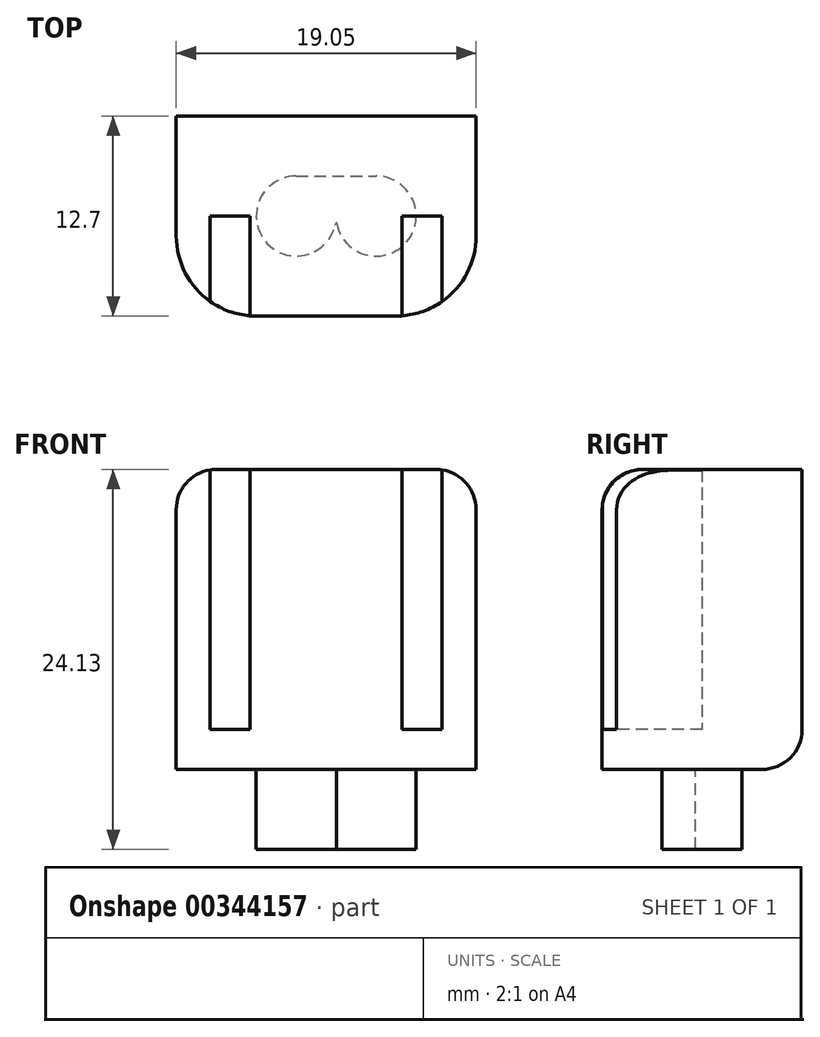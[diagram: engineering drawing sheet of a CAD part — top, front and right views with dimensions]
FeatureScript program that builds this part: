
annotation { "Feature Type Name" : "Feature", "Feature Type Description" : "" }
export const myFeature = defineFeature(function(context is Context, id is Id, definition is map)
    precondition{}
    {
        {
            var Q0;
            Q0=qCreatedBy(makeId("Front.planeOp"),FACE);
            var sketch = newSketch(context, id + "F0", { "sketchPlane" : qUnion([Q0])});
            skLineSegment(sketch, "E0", {"start": v(-9.43, 0) * mm, "end": v(9.62, 0) * mm});
            skLineSegment(sketch, "E1", {"start": v(9.62, 0) * mm, "end": v(9.62, 19.05) * mm});
            skLineSegment(sketch, "E2", {"start": v(9.62, 19.05) * mm, "end": v(-9.43, 19.05) * mm});
            skLineSegment(sketch, "E3", {"start": v(-9.43, 19.05) * mm, "end": v(-9.43, 0) * mm});
            skSolve(sketch);
        }
        {
            var Q0;
            Q0=makeQuery(id+"F0.imprint","IMPRINT",FACE,{"disambiguationData":[TD([[makeQuery(id+"F0.imprint","IMPRINT",EDGE,{"derivedFrom":sQuery(id+"F0.wireOp",EDGE,"E0")}),1.0]])]});
            extrude(context, id + "F1", {"entities" : qUnion([Q0]), "depth" : 12.7 * mm});
        }
        {
            var Q0;
            Q0=makeQuery(id+"F1.opExtrude","SWEPT_EDGE",EDGE,{"disambiguationData":[OSD([sQuery(id+"F0.wireOp",EDGE,"E1"),sQuery(id+"F0.wireOp",EDGE,"E2")])]});
            var Q1;
            Q1=makeQuery(id+"F1.opExtrude","SWEPT_EDGE",EDGE,{"disambiguationData":[OSD([sQuery(id+"F0.wireOp",EDGE,"E2"),sQuery(id+"F0.wireOp",EDGE,"E3")])]});
            var Q2;
            Q2=makeQuery(id+"F1.opExtrude","CAP_EDGE",EDGE,{"disambiguationData":[OSD([sQuery(id+"F0.wireOp",EDGE,"E2")])],"isStart":false});
            fillet(context, id + "F2", {"entities" : qUnion([Q0, Q1, Q2]), "radius" : 2.54 * mm, "tangentPropagation" : true, "allowEdgeOverflow" : false});
        }
        {
            var Q0;
            Q0=makeQuery(id+"F1.opExtrude","CAP_EDGE",EDGE,{"disambiguationData":[OSD([sQuery(id+"F0.wireOp",EDGE,"E1")])],"isStart":false});
            var Q1;
            Q1=makeQuery(id+"F1.opExtrude","CAP_EDGE",EDGE,{"disambiguationData":[OSD([sQuery(id+"F0.wireOp",EDGE,"E3")])],"isStart":false});
            fillet(context, id + "F3", {"entities" : qUnion([Q0, Q1]), "radius" : 5.08 * mm, "tangentPropagation" : true, "allowEdgeOverflow" : false});
        }
        {
            var Q0;
            Q0=makeQuery(id+"F1.opExtrude","CAP_FACE",FACE,{"disambiguationData":[OSD([sQuery(id+"F0.wireOp",EDGE,"E0"),sQuery(id+"F0.wireOp",EDGE,"E1"),sQuery(id+"F0.wireOp",EDGE,"E2"),sQuery(id+"F0.wireOp",EDGE,"E3")])],"isStart":false});
            cPlane(context, id + "F4", {"entities" : qUnion([Q0]), "cplaneType" : CPlaneType.OFFSET, "offset" : 0 * mm, "width" : 152.4 * mm, "height" : 152.4 * mm});
        }
        {
            var Q0;
            Q0=qCreatedBy(id+"F4.planeOp",FACE);
            var sketch = newSketch(context, id + "F5", { "sketchPlane" : qUnion([Q0])});
            skLineSegment(sketch, "E4.bottom", {"start": v(-7.27, 19.05) * mm, "end": v(-4.73, 19.05) * mm});
            skLineSegment(sketch, "E4.top", {"start": v(-7.27, 2.54) * mm, "end": v(-4.73, 2.54) * mm});
            skLineSegment(sketch, "E4.left", {"start": v(-7.27, 19.05) * mm, "end": v(-7.27, 2.54) * mm});
            skLineSegment(sketch, "E4.right", {"start": v(-4.73, 19.05) * mm, "end": v(-4.73, 2.54) * mm});
            skLineSegment(sketch, "E5.bottom", {"start": v(4.92, 19.05) * mm, "end": v(7.46, 19.05) * mm});
            skLineSegment(sketch, "E5.top", {"start": v(4.92, 2.54) * mm, "end": v(7.46, 2.54) * mm});
            skLineSegment(sketch, "E5.left", {"start": v(4.92, 19.05) * mm, "end": v(4.92, 2.54) * mm});
            skLineSegment(sketch, "E5.right", {"start": v(7.46, 19.05) * mm, "end": v(7.46, 2.54) * mm});
            skSolve(sketch);
        }
        {
            var Q0;
            Q0=makeQuery(id+"F5.imprint","IMPRINT",FACE,{"disambiguationData":[TD([[makeQuery(id+"F5.imprint","IMPRINT",EDGE,{"derivedFrom":sQuery(id+"F5.wireOp",EDGE,"E4.bottom")}),-1.0]])]});
            var Q1;
            Q1=makeQuery(id+"F5.imprint","IMPRINT",FACE,{"disambiguationData":[TD([[makeQuery(id+"F5.imprint","IMPRINT",EDGE,{"derivedFrom":sQuery(id+"F5.wireOp",EDGE,"E5.bottom")}),-1.0]])]});
            var Q2;
            Q2=makeQuery(id+"F1.opExtrude","CAP_FACE",FACE,{"disambiguationData":[OSD([sQuery(id+"F0.wireOp",EDGE,"E0"),sQuery(id+"F0.wireOp",EDGE,"E1"),sQuery(id+"F0.wireOp",EDGE,"E2"),sQuery(id+"F0.wireOp",EDGE,"E3")])],"isStart":true});
            extrude(context, id + "F6", {"entities" : qUnion([Q0, Q1]), "operationType" : NewBodyOperationType.REMOVE, "oppositeDirection" : true, "endBoundEntityFace" : qUnion([Q2]), "depth" : 6.35 * mm});
        }
        {
            var Q0;
            Q0=makeQuery(id+"F1.opExtrude","CAP_EDGE",EDGE,{"disambiguationData":[OSD([sQuery(id+"F0.wireOp",EDGE,"E0")])],"isStart":true});
            fillet(context, id + "F7", {"entities" : qUnion([Q0]), "radius" : 2.54 * mm, "tangentPropagation" : true, "allowEdgeOverflow" : false});
        }
        {
            var Q0;
            Q0=makeQuery(id+"F1.opExtrude","SWEPT_FACE",FACE,{"disambiguationData":[OSD([sQuery(id+"F0.wireOp",EDGE,"E0")])]});
            var sketch = newSketch(context, id + "F8", { "sketchPlane" : qUnion([Q0])});
            skArc(sketch, "E6", {"start": v(0.67, 6.93) * mm, "mid": v(-4.35, 6.35) * mm, "end": v(0.67, 5.77) * mm});
            skArc(sketch, "E7", {"start": v(1.63, 4.41) * mm, "mid": v(5.66, 7.23) * mm, "end": v(0.77, 6.76) * mm});
            skLineSegment(sketch, "E8", {"start": v(-2.9, 3.81) * mm, "end": v(4.45, 3.81) * mm});
            skArc(sketch, "E9", {"start": v(0.67, 6.93) * mm, "mid": v(0.7, 6.84) * mm, "end": v(0.77, 6.76) * mm});
            skSolve(sketch);
        }
        {
            var Q0;
            {var subQ0=sQuery(id+"F8.wireOp",EDGE,"E9");Q0=makeQuery(id+"F8.imprint","IMPRINT",FACE,{"disambiguationData":[TD([[makeQuery(id+"F8.imprint","IMPRINT",EDGE,{"derivedFrom":subQ0}),-1.0]])]});}
            extrude(context, id + "F9", {"entities" : qUnion([Q0]), "operationType" : NewBodyOperationType.ADD, "depth" : 5.08 * mm});
        }
    });
